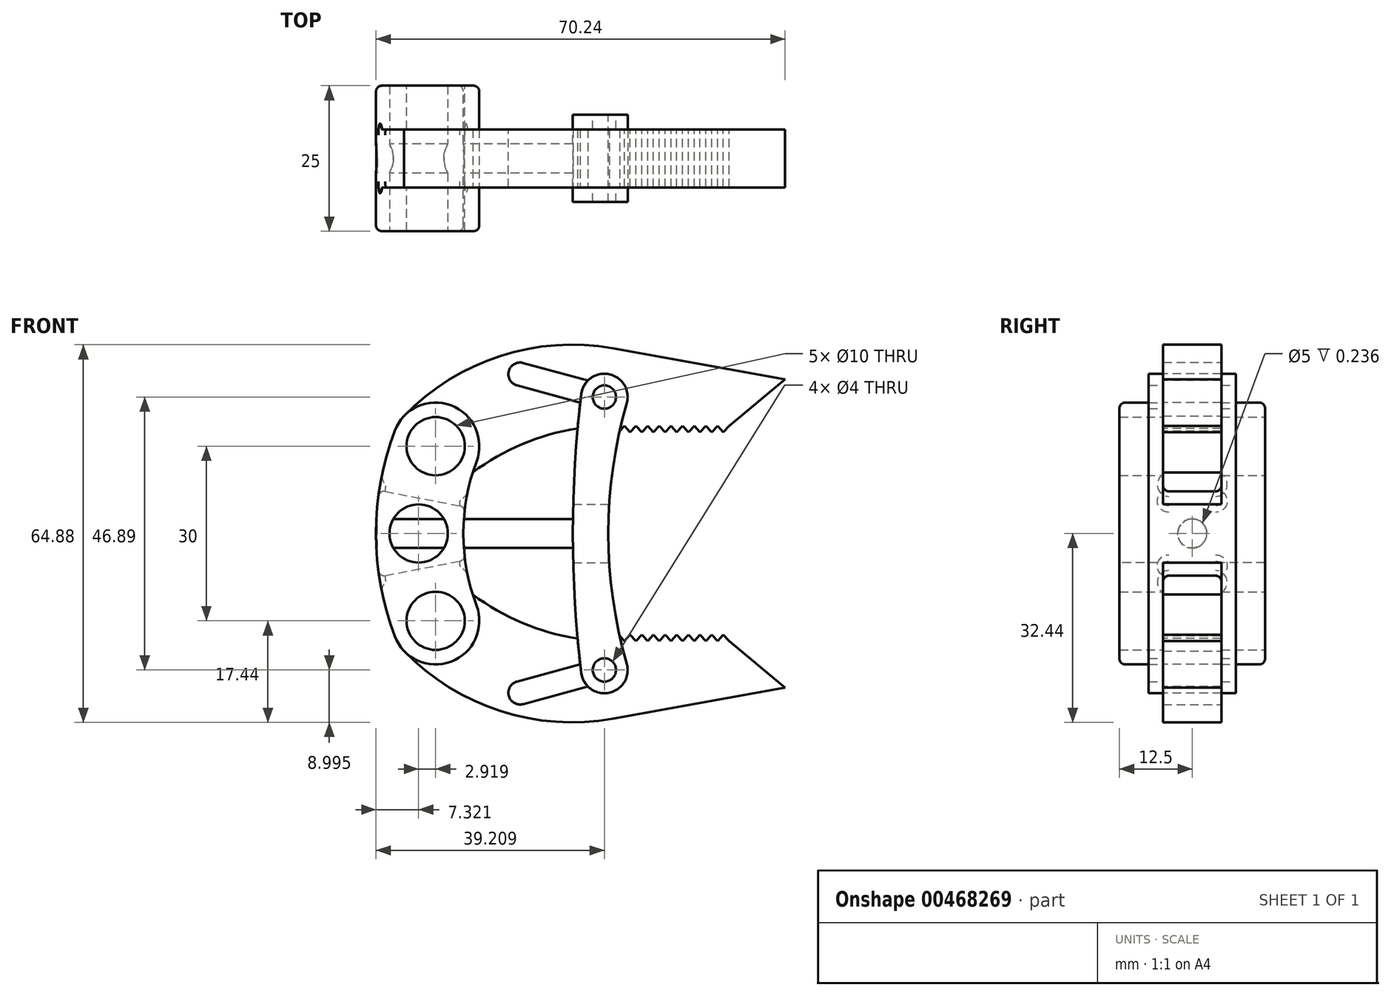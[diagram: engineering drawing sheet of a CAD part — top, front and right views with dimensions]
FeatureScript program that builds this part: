
annotation { "Feature Type Name" : "Feature", "Feature Type Description" : "" }
export const myFeature = defineFeature(function(context is Context, id is Id, definition is map)
    precondition{}
    {
        {
            var Q0;
            Q0=qCreatedBy(makeId("Front.planeOp"),FACE);
            var sketch = newSketch(context, id + "F0", { "sketchPlane" : qUnion([Q0])});
            skLineSegment(sketch, "E0", {"start": v(0, 15) * mm, "end": v(0, -15) * mm, "construction": true});
            skLineSegment(sketch, "E1", {"start": v(0, 0) * mm, "end": v(39.76, 0) * mm, "construction": true});
            skCircle(sketch, "E2", {"center": v(0, 15) * mm, "radius": 5 * mm});
            skCircle(sketch, "E3", {"center": v(0, -15) * mm, "radius": 5 * mm});
            skArc(sketch, "E4", {"start": v(-7.02, 17.65) * mm, "mid": v(-10.24, 0) * mm, "end": v(-7.02, -17.65) * mm});
            skCircle(sketch, "E5.0", {"center": v(0, 15) * mm, "radius": 7.5 * mm});
            skCircle(sketch, "E6.0", {"center": v(0, -15) * mm, "radius": 7.5 * mm});
            skArc(sketch, "E7", {"start": v(7.02, 12.35) * mm, "mid": v(4.76, 0) * mm, "end": v(7.02, -12.35) * mm});
            skSolve(sketch);
        }
        {
            var Q0;
            Q0=qCreatedBy(makeId("Front.planeOp"),FACE);
            var sketch = newSketch(context, id + "F1", { "sketchPlane" : qUnion([Q0])});
            skCircle(sketch, "E8.0", {"center": v(0, 15) * mm, "radius": 5 * mm});
            skArc(sketch, "E9", {"start": v(30.47, 31.81) * mm, "mid": v(11.08, 30.5) * mm, "end": v(-5.4, 20.2) * mm});
            skArc(sketch, "E10", {"start": v(30.4, 18.5) * mm, "mid": v(16.79, 16.12) * mm, "end": v(4.8, 9.24) * mm});
            skLineSegment(sketch, "E11", {"start": v(30.4, 18.5) * mm, "end": v(30.4, 18.5) * mm});
            skLineSegment(sketch, "E12", {"start": v(50.4, 18.5) * mm, "end": v(60, 26.5) * mm});
            skLineSegment(sketch, "E13", {"start": v(60, 26.5) * mm, "end": v(30.47, 31.81) * mm});
            skArc(sketch, "E14.0", {"start": v(-5.4, 20.2) * mm, "mid": v(-5.5, 9.9) * mm, "end": v(4.8, 9.24) * mm});
            skLineSegment(sketch, "E15", {"start": v(30.47, 31.81) * mm, "end": v(28.97, 23.45) * mm, "construction": true});
            skLineSegment(sketch, "E16", {"start": v(28.97, 23.45) * mm, "end": v(14.5, 27.38) * mm, "construction": true});
            skLineSegment(sketch, "E17", {"start": v(0, 0) * mm, "end": v(65.72, 0) * mm, "construction": true});
            skCircle(sketch, "E18", {"center": v(14.5, 27.38) * mm, "radius": 2 * mm});
            skCircle(sketch, "E19", {"center": v(28.97, 23.45) * mm, "radius": 2 * mm});
            skLineSegment(sketch, "E20", {"start": v(15.02, 29.3) * mm, "end": v(29.5, 25.38) * mm});
            skLineSegment(sketch, "E21", {"start": v(13.97, 25.45) * mm, "end": v(28.45, 21.51) * mm});
            skLineSegment(sketch, "E22", {"start": v(30.4, 18.5) * mm, "end": v(32.4, 18.5) * mm, "construction": true});
            skLineSegment(sketch, "E23", {"start": v(32.4, 18.5) * mm, "end": v(34.4, 18.5) * mm, "construction": true});
            skLineSegment(sketch, "E24", {"start": v(34.4, 18.5) * mm, "end": v(36.4, 18.5) * mm, "construction": true});
            skLineSegment(sketch, "E25", {"start": v(36.4, 18.5) * mm, "end": v(38.4, 18.5) * mm, "construction": true});
            skLineSegment(sketch, "E26", {"start": v(38.4, 18.5) * mm, "end": v(40.4, 18.5) * mm, "construction": true});
            skLineSegment(sketch, "E27", {"start": v(40.4, 18.5) * mm, "end": v(42.4, 18.5) * mm, "construction": true});
            skLineSegment(sketch, "E28", {"start": v(42.4, 18.5) * mm, "end": v(44.4, 18.5) * mm, "construction": true});
            skLineSegment(sketch, "E29", {"start": v(44.4, 18.5) * mm, "end": v(46.4, 18.5) * mm, "construction": true});
            skLineSegment(sketch, "E30", {"start": v(46.4, 18.5) * mm, "end": v(48.4, 18.5) * mm, "construction": true});
            skLineSegment(sketch, "E31", {"start": v(48.4, 18.5) * mm, "end": v(50.4, 18.5) * mm, "construction": true});
            skLineSegment(sketch, "E32", {"start": v(30.4, 18.5) * mm, "end": v(31.4, 17.39) * mm});
            skLineSegment(sketch, "E33", {"start": v(31.4, 17.39) * mm, "end": v(32.4, 18.5) * mm});
            skLineSegment(sketch, "E34", {"start": v(32.4, 18.5) * mm, "end": v(33.4, 17.39) * mm});
            skLineSegment(sketch, "E35", {"start": v(33.4, 17.39) * mm, "end": v(34.4, 18.5) * mm});
            skLineSegment(sketch, "E36", {"start": v(34.4, 18.5) * mm, "end": v(35.4, 17.39) * mm});
            skLineSegment(sketch, "E37", {"start": v(35.4, 17.39) * mm, "end": v(36.4, 18.5) * mm});
            skLineSegment(sketch, "E38", {"start": v(36.4, 18.5) * mm, "end": v(37.4, 17.39) * mm});
            skLineSegment(sketch, "E39", {"start": v(37.4, 17.39) * mm, "end": v(38.4, 18.5) * mm});
            skLineSegment(sketch, "E40", {"start": v(38.4, 18.5) * mm, "end": v(39.4, 17.39) * mm});
            skLineSegment(sketch, "E41", {"start": v(39.4, 17.39) * mm, "end": v(40.4, 18.5) * mm});
            skLineSegment(sketch, "E42", {"start": v(40.4, 18.5) * mm, "end": v(41.4, 17.39) * mm});
            skLineSegment(sketch, "E43", {"start": v(41.4, 17.39) * mm, "end": v(42.4, 18.5) * mm});
            skLineSegment(sketch, "E44", {"start": v(42.4, 18.5) * mm, "end": v(43.4, 17.39) * mm});
            skLineSegment(sketch, "E45", {"start": v(43.4, 17.39) * mm, "end": v(44.4, 18.5) * mm});
            skLineSegment(sketch, "E46", {"start": v(44.4, 18.5) * mm, "end": v(45.4, 17.39) * mm});
            skLineSegment(sketch, "E47", {"start": v(45.4, 17.39) * mm, "end": v(46.4, 18.5) * mm});
            skLineSegment(sketch, "E48", {"start": v(46.4, 18.5) * mm, "end": v(47.4, 17.39) * mm});
            skLineSegment(sketch, "E49", {"start": v(47.4, 17.39) * mm, "end": v(48.4, 18.5) * mm});
            skLineSegment(sketch, "E50", {"start": v(48.4, 18.5) * mm, "end": v(49.4, 17.39) * mm});
            skLineSegment(sketch, "E51", {"start": v(49.4, 17.39) * mm, "end": v(50.4, 18.5) * mm});
            skArc(sketch, "E52.MirrorCS", {"start": v(-5.4, -20.2) * mm, "mid": v(-5.5, -9.9) * mm, "end": v(4.8, -9.24) * mm});
            skLineSegment(sketch, "E53.MirrorCS", {"start": v(32.4, -18.5) * mm, "end": v(34.4, -18.5) * mm, "construction": true});
            skLineSegment(sketch, "E54.MirrorCS", {"start": v(30.4, -18.5) * mm, "end": v(32.4, -18.5) * mm, "construction": true});
            skLineSegment(sketch, "E55.MirrorCS", {"start": v(40.4, -18.5) * mm, "end": v(41.4, -17.39) * mm});
            skLineSegment(sketch, "E56.MirrorCS", {"start": v(44.4, -18.5) * mm, "end": v(46.4, -18.5) * mm, "construction": true});
            skLineSegment(sketch, "E57.MirrorCS", {"start": v(38.4, -18.5) * mm, "end": v(40.4, -18.5) * mm, "construction": true});
            skLineSegment(sketch, "E58.MirrorCS", {"start": v(46.4, -18.5) * mm, "end": v(48.4, -18.5) * mm, "construction": true});
            skLineSegment(sketch, "E59.MirrorCS", {"start": v(41.4, -17.39) * mm, "end": v(42.4, -18.5) * mm});
            skLineSegment(sketch, "E60.MirrorCS", {"start": v(36.4, -18.5) * mm, "end": v(38.4, -18.5) * mm, "construction": true});
            skLineSegment(sketch, "E61.MirrorCS", {"start": v(40.4, -18.5) * mm, "end": v(42.4, -18.5) * mm, "construction": true});
            skLineSegment(sketch, "E62.MirrorCS", {"start": v(34.4, -18.5) * mm, "end": v(36.4, -18.5) * mm, "construction": true});
            skLineSegment(sketch, "E63.MirrorCS", {"start": v(42.4, -18.5) * mm, "end": v(44.4, -18.5) * mm, "construction": true});
            skLineSegment(sketch, "E64.MirrorCS", {"start": v(30.4, -18.5) * mm, "end": v(31.4, -17.39) * mm});
            skLineSegment(sketch, "E65.MirrorCS", {"start": v(34.4, -18.5) * mm, "end": v(35.4, -17.39) * mm});
            skLineSegment(sketch, "E66.MirrorCS", {"start": v(38.4, -18.5) * mm, "end": v(39.4, -17.39) * mm});
            skLineSegment(sketch, "E67.MirrorCS", {"start": v(48.4, -18.5) * mm, "end": v(50.4, -18.5) * mm, "construction": true});
            skLineSegment(sketch, "E68.MirrorCS", {"start": v(32.4, -18.5) * mm, "end": v(33.4, -17.39) * mm});
            skLineSegment(sketch, "E69.MirrorCS", {"start": v(48.4, -18.5) * mm, "end": v(49.4, -17.39) * mm});
            skLineSegment(sketch, "E70.MirrorCS", {"start": v(44.4, -18.5) * mm, "end": v(45.4, -17.39) * mm});
            skLineSegment(sketch, "E71.MirrorCS", {"start": v(33.4, -17.39) * mm, "end": v(34.4, -18.5) * mm});
            skLineSegment(sketch, "E72.MirrorCS", {"start": v(31.4, -17.39) * mm, "end": v(32.4, -18.5) * mm});
            skLineSegment(sketch, "E73.MirrorCS", {"start": v(43.4, -17.39) * mm, "end": v(44.4, -18.5) * mm});
            skLineSegment(sketch, "E74.MirrorCS", {"start": v(35.4, -17.39) * mm, "end": v(36.4, -18.5) * mm});
            skLineSegment(sketch, "E75.MirrorCS", {"start": v(37.4, -17.39) * mm, "end": v(38.4, -18.5) * mm});
            skLineSegment(sketch, "E76.MirrorCS", {"start": v(45.4, -17.39) * mm, "end": v(46.4, -18.5) * mm});
            skLineSegment(sketch, "E77.MirrorCS", {"start": v(46.4, -18.5) * mm, "end": v(47.4, -17.39) * mm});
            skLineSegment(sketch, "E78.MirrorCS", {"start": v(39.4, -17.39) * mm, "end": v(40.4, -18.5) * mm});
            skLineSegment(sketch, "E79.MirrorCS", {"start": v(42.4, -18.5) * mm, "end": v(43.4, -17.39) * mm});
            skLineSegment(sketch, "E80.MirrorCS", {"start": v(49.4, -17.39) * mm, "end": v(50.4, -18.5) * mm});
            skLineSegment(sketch, "E81.MirrorCS", {"start": v(47.4, -17.39) * mm, "end": v(48.4, -18.5) * mm});
            skLineSegment(sketch, "E82.MirrorCS", {"start": v(36.4, -18.5) * mm, "end": v(37.4, -17.39) * mm});
            skLineSegment(sketch, "E83.MirrorCS", {"start": v(30.47, -31.81) * mm, "end": v(28.97, -23.45) * mm, "construction": true});
            skLineSegment(sketch, "E84.MirrorCS", {"start": v(28.97, -23.45) * mm, "end": v(14.5, -27.38) * mm, "construction": true});
            skCircle(sketch, "E85.MirrorC", {"center": v(14.5, -27.38) * mm, "radius": 2 * mm});
            skCircle(sketch, "E86.MirrorC", {"center": v(28.97, -23.45) * mm, "radius": 2 * mm});
            skLineSegment(sketch, "E87.MirrorCS", {"start": v(15.02, -29.3) * mm, "end": v(29.5, -25.38) * mm});
            skLineSegment(sketch, "E88.MirrorCS", {"start": v(13.97, -25.45) * mm, "end": v(28.45, -21.51) * mm});
            skCircle(sketch, "E89.MirrorC", {"center": v(0, -15) * mm, "radius": 5 * mm});
            skArc(sketch, "E90.MirrorCS", {"start": v(30.4, -18.5) * mm, "mid": v(16.79, -16.12) * mm, "end": v(4.8, -9.24) * mm});
            skLineSegment(sketch, "E91.MirrorCS", {"start": v(60, -26.5) * mm, "end": v(30.47, -31.81) * mm});
            skArc(sketch, "E92.MirrorCS", {"start": v(30.47, -31.81) * mm, "mid": v(11.08, -30.5) * mm, "end": v(-5.4, -20.2) * mm});
            skLineSegment(sketch, "E93.MirrorCS", {"start": v(50.4, -18.5) * mm, "end": v(60, -26.5) * mm});
            skSolve(sketch);
        }
        {
            var Q0;
            Q0=qSketchRegion(id+"F0",true);
            extrude(context, id + "F2", {"entities" : qUnion([Q0]), "endBound" : BoundingType.SYMMETRIC, "depth" : 25 * mm});
        }
        {
            var Q0;
            Q0=qSketchRegion(id+"F1",true);
            extrude(context, id + "F3", {"entities" : qUnion([Q0]), "endBound" : BoundingType.SYMMETRIC, "depth" : 10 * mm});
        }
        {
            var Q0;
            Q0=makeQuery(id+"F2.opExtrude","CAP_FACE",FACE,{"disambiguationData":[OSD([sQuery(id+"F0.wireOp",EDGE,"E2"),sQuery(id+"F0.wireOp",EDGE,"E3"),sQuery(id+"F0.wireOp",EDGE,"E4"),sQuery(id+"F0.wireOp",EDGE,"E5.0"),sQuery(id+"F0.wireOp",EDGE,"E6.0"),sQuery(id+"F0.wireOp",EDGE,"E7")])],"isStart":false});
            var sketch = newSketch(context, id + "F4", { "sketchPlane" : qUnion([Q0])});
            skCircle(sketch, "E94", {"center": v(0, 15) * mm, "radius": 5 * mm});
            skCircle(sketch, "E95", {"center": v(0, -15) * mm, "radius": 5 * mm});
            skArc(sketch, "E96", {"start": v(0, 15) * mm, "mid": v(-2.92, 0) * mm, "end": v(0, -15) * mm, "construction": true});
            skCircle(sketch, "E97", {"center": v(-2.92, 0) * mm, "radius": 5 * mm});
            skSolve(sketch);
        }
        {
            var Q0;
            Q0=makeQuery(id+"F4.imprint","IMPRINT",FACE,{"disambiguationData":[TD([[makeQuery(id+"F4.imprint","IMPRINT",EDGE,{"derivedFrom":sQuery(id+"F4.wireOp",EDGE,"E97")}),1.0]])]});
            extrude(context, id + "F5", {"entities" : qUnion([Q0]), "operationType" : NewBodyOperationType.REMOVE, "endBound" : BoundingType.THROUGH_ALL, "oppositeDirection" : true, "depth" : 25 * mm});
        }
        {
            var Q0;
            Q0=qCreatedBy(makeId("Front.planeOp"),FACE);
            var sketch = newSketch(context, id + "F6", { "sketchPlane" : qUnion([Q0])});
            skCircle(sketch, "E98", {"center": v(-2.92, 0) * mm, "radius": 5 * mm});
            skCircle(sketch, "E99", {"center": v(0, 15) * mm, "radius": 5 * mm});
            skCircle(sketch, "E100.0", {"center": v(-2.92, 0) * mm, "radius": 6 * mm, "construction": true});
            skCircle(sketch, "E101", {"center": v(0, 15) * mm, "radius": 9.28 * mm, "construction": true});
            skLineSegment(sketch, "E102", {"start": v(0, 15) * mm, "end": v(-2.92, 0) * mm, "construction": true});
            skLineSegment(sketch, "E103", {"start": v(-2.92, 0) * mm, "end": v(25, 0) * mm, "construction": true});
            skLineSegment(sketch, "E104", {"start": v(-9.68, 7.43) * mm, "end": v(5.06, 4.56) * mm});
            skLineSegment(sketch, "E105.MirrorCS", {"start": v(-9.68, -7.43) * mm, "end": v(5.06, -4.56) * mm});
            skArc(sketch, "E106", {"start": v(7.02, 12.35) * mm, "mid": v(5.82, 8.51) * mm, "end": v(5.06, 4.56) * mm});
            skArc(sketch, "E107", {"start": v(-7.02, 17.65) * mm, "mid": v(-8.62, 12.6) * mm, "end": v(-9.68, 7.43) * mm});
            skArc(sketch, "E108.MirrorCS", {"start": v(7.02, -12.35) * mm, "mid": v(5.82, -8.51) * mm, "end": v(5.06, -4.56) * mm});
            skArc(sketch, "E109.MirrorCS", {"start": v(-7.02, -17.65) * mm, "mid": v(-8.62, -12.6) * mm, "end": v(-9.68, -7.43) * mm});
            skArc(sketch, "E110", {"start": v(-7.02, -17.65) * mm, "mid": v(2.65, -22.02) * mm, "end": v(7.02, -12.35) * mm});
            skArc(sketch, "E111", {"start": v(7.02, 12.35) * mm, "mid": v(2.65, 22.02) * mm, "end": v(-7.02, 17.65) * mm});
            skSolve(sketch);
        }
        {
            var Q0;
            Q0=qSketchRegion(id+"F6",true);
            var Q1;
            Q1=sQuery(id+"F6.wireOp",EDGE,"E104");
            var Q2;
            Q2=sQuery(id+"F6.wireOp",EDGE,"E107");
            var Q3;
            Q3=sQuery(id+"F6.wireOp",EDGE,"E111");
            var Q4;
            Q4=sQuery(id+"F6.wireOp",EDGE,"E106");
            var Q5;
            Q5=sQuery(id+"F6.wireOp",EDGE,"E108.MirrorCS");
            var Q6;
            Q6=sQuery(id+"F6.wireOp",EDGE,"E110");
            var Q7;
            Q7=sQuery(id+"F6.wireOp",EDGE,"E105.MirrorCS");
            var Q8;
            Q8=sQuery(id+"F6.wireOp",EDGE,"E109.MirrorCS");
            extrude(context, id + "F7", {"entities" : qUnion([Q0]), "operationType" : NewBodyOperationType.REMOVE, "surfaceEntities" : qUnion([Q1, Q2, Q3, Q4, Q5, Q6, Q7, Q8]), "endBound" : BoundingType.SYMMETRIC, "oppositeDirection" : true, "depth" : 10 * mm});
        }
        {
            var Q0;
            Q0=qCreatedBy(makeId("Right.planeOp"),FACE);
            var sketch = newSketch(context, id + "F8", { "sketchPlane" : qUnion([Q0])});
            skCircle(sketch, "E112", {"center": v(0, 0) * mm, "radius": 2.5 * mm});
            skSolve(sketch);
        }
        {
            var Q0;
            Q0=qSketchRegion(id+"F8",true);
            extrude(context, id + "F9", {"entities" : qUnion([Q0]), "operationType" : NewBodyOperationType.REMOVE, "endBound" : BoundingType.THROUGH_ALL, "depth" : 25 * mm, "hasSecondDirection" : true, "secondDirectionBound" : SecondDirectionBoundingType.THROUGH_ALL, "secondDirectionOppositeDirection" : true, "secondDirectionDepth" : 25 * mm});
        }
        {
            var Q0;
            Q0=qSketchRegion(id+"F8",true);
            extrude(context, id + "F10", {"entities" : qUnion([Q0]), "depth" : 27 * mm, "hasSecondDirection" : true, "secondDirectionOppositeDirection" : true, "secondDirectionDepth" : 10 * mm});
        }
        {
            var Q0;
            Q0=qCreatedBy(makeId("Front.planeOp"),FACE);
            var sketch = newSketch(context, id + "F11", { "sketchPlane" : qUnion([Q0])});
            skCircle(sketch, "E113", {"center": v(28.97, 23.45) * mm, "radius": 2 * mm});
            skCircle(sketch, "E114", {"center": v(28.97, -23.45) * mm, "radius": 2 * mm});
            skCircle(sketch, "E115", {"center": v(28.97, 23.45) * mm, "radius": 4 * mm});
            skCircle(sketch, "E116", {"center": v(28.97, -23.45) * mm, "radius": 4 * mm});
            skArc(sketch, "E117", {"start": v(32.81, 22.33) * mm, "mid": v(29.63, 0) * mm, "end": v(32.81, -22.33) * mm});
            skArc(sketch, "E118", {"start": v(25, 23.92) * mm, "mid": v(23.56, 0) * mm, "end": v(25, -23.92) * mm});
            skLineSegment(sketch, "E119", {"start": v(0.5, 0) * mm, "end": v(51.97, 0) * mm, "construction": true});
            skLineSegment(sketch, "E120", {"start": v(28.97, 23.45) * mm, "end": v(28.97, -23.45) * mm, "construction": true});
            skSolve(sketch);
        }
        {
            var Q0;
            Q0=qSketchRegion(id+"F11",true);
            extrude(context, id + "F12", {"entities" : qUnion([Q0]), "endBound" : BoundingType.SYMMETRIC, "depth" : 15 * mm});
        }
        {
            var Q0;
            Q0=qCreatedBy(makeId("Front.planeOp"),FACE);
            var sketch = newSketch(context, id + "F13", { "sketchPlane" : qUnion([Q0])});
            skLineSegment(sketch, "E121", {"start": v(23.62, 5) * mm, "end": v(29.79, 5) * mm});
            skLineSegment(sketch, "E122", {"start": v(23.62, -5) * mm, "end": v(29.79, -5) * mm});
            skLineSegment(sketch, "E123", {"start": v(14.44, 0) * mm, "end": v(35.78, 0) * mm, "construction": true});
            skArc(sketch, "E124.0.0", {"start": v(32.81, 22.33) * mm, "mid": v(29.77, 27.36) * mm, "end": v(25, 23.92) * mm});
            skArc(sketch, "E124.0.1", {"start": v(25, 23.92) * mm, "mid": v(24.09, 14.48) * mm, "end": v(23.62, 5) * mm});
            skArc(sketch, "E124.0.2", {"start": v(25, -23.92) * mm, "mid": v(29.77, -27.36) * mm, "end": v(32.81, -22.33) * mm});
            skArc(sketch, "E124.0.3", {"start": v(32.81, -22.33) * mm, "mid": v(30.82, -13.75) * mm, "end": v(29.79, -5) * mm});
            skArc(sketch, "E125.trimOffspring", {"start": v(29.79, 5) * mm, "mid": v(30.82, 13.75) * mm, "end": v(32.81, 22.33) * mm});
            skArc(sketch, "E126.trimOffspring", {"start": v(23.62, -5) * mm, "mid": v(24.09, -14.48) * mm, "end": v(25, -23.92) * mm});
            skSolve(sketch);
        }
        {
            var Q0;
            Q0=qSketchRegion(id+"F13",true);
            var Q1;
            Q1=sQuery(id+"F13.wireOp",EDGE,"E124.0.1");
            var Q2;
            Q2=sQuery(id+"F13.wireOp",EDGE,"E125.trimOffspring");
            var Q3;
            Q3=sQuery(id+"F13.wireOp",EDGE,"E121");
            var Q4;
            Q4=sQuery(id+"F13.wireOp",EDGE,"E124.0.0");
            var Q5;
            Q5=sQuery(id+"F13.wireOp",EDGE,"E126.trimOffspring");
            var Q6;
            Q6=sQuery(id+"F13.wireOp",EDGE,"E124.0.3");
            var Q7;
            Q7=sQuery(id+"F13.wireOp",EDGE,"E124.0.2");
            var Q8;
            Q8=sQuery(id+"F13.wireOp",EDGE,"E122");
            extrude(context, id + "F14", {"entities" : qUnion([Q0]), "operationType" : NewBodyOperationType.REMOVE, "surfaceEntities" : qUnion([Q1, Q2, Q3, Q4, Q5, Q6, Q7, Q8]), "endBound" : BoundingType.SYMMETRIC, "oppositeDirection" : true, "depth" : 10 * mm});
        }
        {
            var Q0;
            Q0=makeQuery(id+"F2.opExtrude","CAP_EDGE",EDGE,{"disambiguationData":[OSD([sQuery(id+"F0.wireOp",EDGE,"E7")])],"isStart":true});
            var Q1;
            Q1=makeQuery(id+"F2.opExtrude","CAP_EDGE",EDGE,{"disambiguationData":[OSD([sQuery(id+"F0.wireOp",EDGE,"E7")])],"isStart":false});
            var Q2;
            Q2=makeQuery(id+"F7.boolean.opBoolean","COPY",FACE,{"derivedFrom":makeQuery(id+"F7.opExtrude","SWEPT_FACE",FACE,{"disambiguationData":[OSD([sQuery(id+"F6.wireOp",EDGE,"E104")])]})});
            var Q3;
            Q3=makeQuery(id+"F7.boolean.opBoolean","COPY",FACE,{"derivedFrom":makeQuery(id+"F7.opExtrude","SWEPT_FACE",FACE,{"disambiguationData":[OSD([sQuery(id+"F6.wireOp",EDGE,"E105.MirrorCS")])]})});
            var Q4;
            Q4=makeQuery(id+"F7.boolean.opBoolean","COPY",EDGE,{"derivedFrom":makeQuery(id+"F7.opExtrude","CAP_EDGE",EDGE,{"disambiguationData":[OSD([sQuery(id+"F6.wireOp",EDGE,"E106")])],"isStart":false})});
            fillet(context, id + "F15", {"entities" : qUnion([Q0, Q1, Q2, Q3, Q4]), "radius" : 1 * mm, "tangentPropagation" : true, "allowEdgeOverflow" : false});
        }
        {
            var Q0;
            Q0=makeQuery(id+"F10.opExtrude","SWEPT_BODY",BODY,{"disambiguationData":[OSD([sQuery(id+"F8.wireOp",EDGE,"E112")])]});
            deleteBodies(context, id + "F16", {"entities" : qUnion([Q0])});
        }
        {
            var Q0;
            Q0=qCreatedBy(makeId("Right.planeOp"),FACE);
            var sketch = newSketch(context, id + "F17", { "sketchPlane" : qUnion([Q0])});
            skCircle(sketch, "E127", {"center": v(0, 0) * mm, "radius": 2.5 * mm});
            skSolve(sketch);
        }
        {
            var Q0;
            Q0=qSketchRegion(id+"F17",true);
            extrude(context, id + "F18", {"entities" : qUnion([Q0]), "operationType" : NewBodyOperationType.ADD, "depth" : 27 * mm, "hasSecondDirection" : true, "secondDirectionOppositeDirection" : true, "secondDirectionDepth" : 10 * mm});
        }
    });
